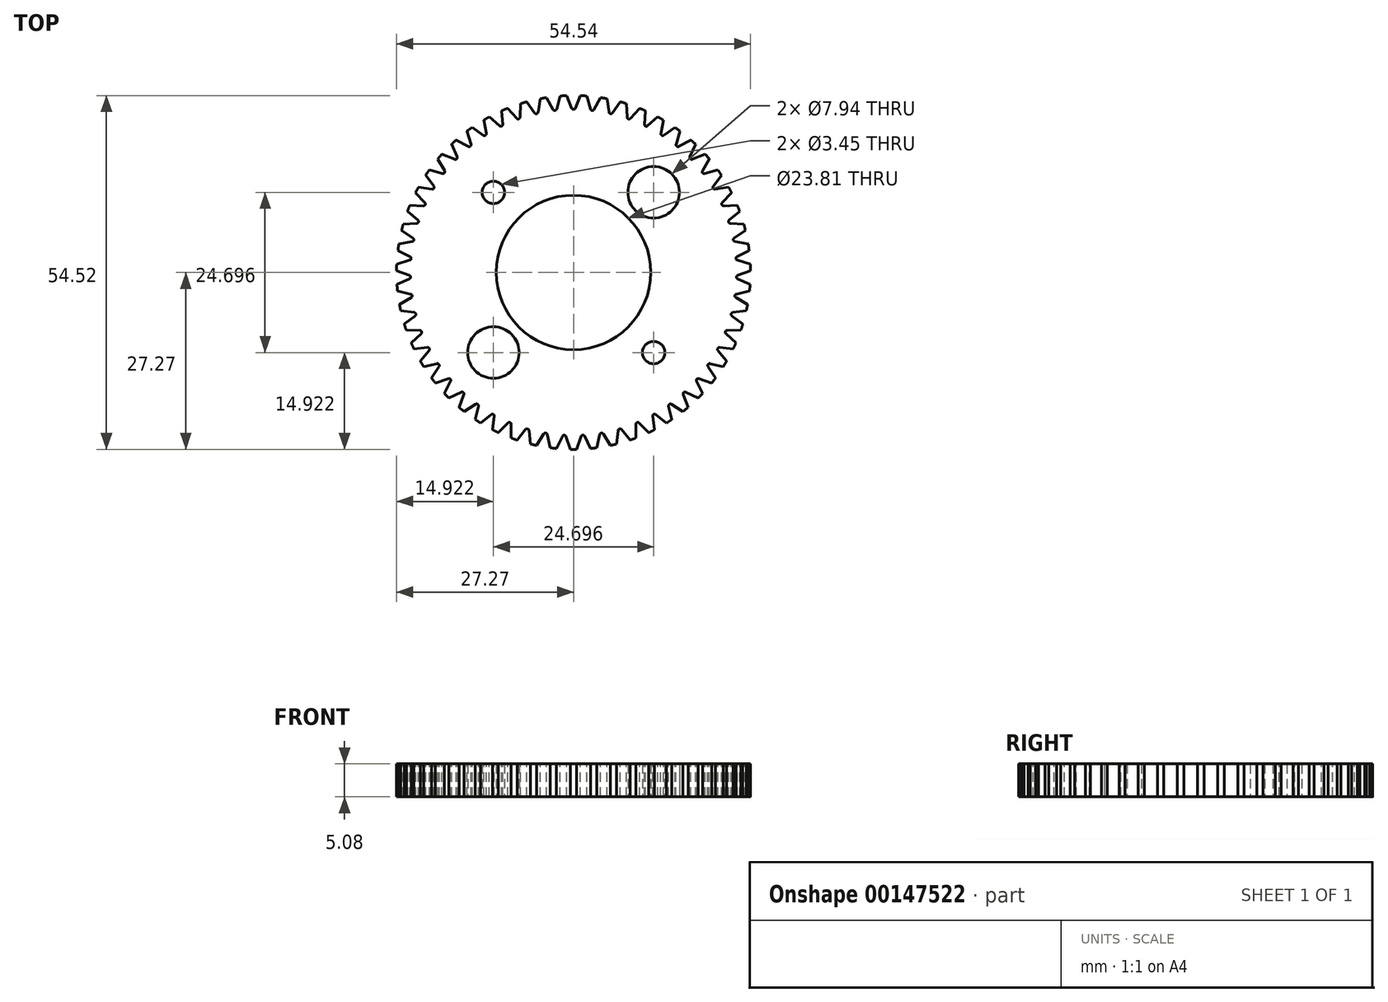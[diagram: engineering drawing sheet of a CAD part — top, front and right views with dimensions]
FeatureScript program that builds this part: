
annotation { "Feature Type Name" : "Feature", "Feature Type Description" : "" }
export const myFeature = defineFeature(function(context is Context, id is Id, definition is map)
    precondition{}
    {
        {
            var Q0;
            Q0=qCreatedBy(makeId("Top.planeOp"),FACE);
            var sketch = newSketch(context, id + "F0", { "sketchPlane" : qUnion([Q0])});
            skCircle(sketch, "E0", {"center": v(0, 0) * mm, "radius": 27.27 * mm});
            skCircle(sketch, "E1", {"center": v(0, 0) * mm, "radius": 11.9 * mm});
            skLineSegment(sketch, "E2.bottom", {"start": v(12.35, -12.35) * mm, "end": v(-12.35, -12.35) * mm, "construction": true});
            skLineSegment(sketch, "E2.top", {"start": v(12.35, 12.35) * mm, "end": v(-12.35, 12.35) * mm, "construction": true});
            skLineSegment(sketch, "E2.left", {"start": v(12.35, -12.35) * mm, "end": v(12.35, 12.35) * mm, "construction": true});
            skLineSegment(sketch, "E2.right", {"start": v(-12.35, -12.35) * mm, "end": v(-12.35, 12.35) * mm, "construction": true});
            skCircle(sketch, "E3", {"center": v(12.35, -12.35) * mm, "radius": 5.56 * mm, "construction": true});
            skCircle(sketch, "E4", {"center": v(12.35, 12.35) * mm, "radius": 3.97 * mm});
            skCircle(sketch, "E5", {"center": v(-12.35, -12.35) * mm, "radius": 3.97 * mm});
            skCircle(sketch, "E6", {"center": v(12.35, -12.35) * mm, "radius": 1.73 * mm});
            skCircle(sketch, "E7", {"center": v(-12.35, 12.35) * mm, "radius": 1.73 * mm});
            skSolve(sketch);
        }
        {
            var Q0;
            Q0=qSketchRegion(id+"F0",true);
            extrude(context, id + "F1", {"entities" : qUnion([Q0]), "depth" : 5.08 * mm});
        }
        {
            var Q0;
            Q0=makeQuery(id+"F1.opExtrude","CAP_FACE",FACE,{"disambiguationData":[OSD([sQuery(id+"F0.wireOp",EDGE,"E0")])],"isStart":false});
            var sketch = newSketch(context, id + "F2", { "sketchPlane" : qUnion([Q0])});
            skLineSegment(sketch, "E8", {"start": v(0, 0) * mm, "end": v(0, 27.27) * mm});
            skArc(sketch, "E9", {"start": v(1.06, 27.25) * mm, "mid": v(0, 27.27) * mm, "end": v(-1.06, 27.25) * mm});
            skLineSegment(sketch, "E10", {"start": v(-1.06, 27.25) * mm, "end": v(-0.28, 25.31) * mm});
            skLineSegment(sketch, "E11", {"start": v(1.06, 27.25) * mm, "end": v(0.28, 25.31) * mm});
            skArc(sketch, "E12", {"start": v(-0.28, 25.31) * mm, "mid": v(0, 25.13) * mm, "end": v(0.28, 25.31) * mm});
            skLineSegment(sketch, "E13", {"start": v(0, 0) * mm, "end": v(0.7, 27.27) * mm, "construction": true});
            skPoint(sketch, "E14", {"position": v(0.67, 26.28) * mm});
            skSolve(sketch);
        }
        {
            var Q0;
            Q0=qSketchRegion(id+"F2",true);
            var Q1;
            Q1=makeQuery(id+"F1.opExtrude","CAP_FACE",FACE,{"disambiguationData":[OSD([sQuery(id+"F0.wireOp",EDGE,"E0")])],"isStart":true});
            extrude(context, id + "F3", {"entities" : qUnion([Q0]), "operationType" : NewBodyOperationType.REMOVE, "endBound" : BoundingType.UP_TO_SURFACE, "oppositeDirection" : true, "endBoundEntityFace" : qUnion([Q1]), "depth" : 25.4 * mm});
        }
        {
            var Q0;
            Q0=makeQuery(id+"F3.boolean.opBoolean","COPY",FACE,{"derivedFrom":makeQuery(id+"F3.opExtrude","SWEPT_FACE",FACE,{"disambiguationData":[OSD([sQuery(id+"F2.wireOp",EDGE,"E11")])]})});
            var Q1;
            Q1=makeQuery(id+"F3.boolean.opBoolean","COPY",FACE,{"derivedFrom":makeQuery(id+"F3.opExtrude","SWEPT_FACE",FACE,{"disambiguationData":[OSD([sQuery(id+"F2.wireOp",EDGE,"E12")])]})});
            var Q2;
            Q2=makeQuery(id+"F3.boolean.opBoolean","COPY",FACE,{"derivedFrom":makeQuery(id+"F3.opExtrude","SWEPT_FACE",FACE,{"disambiguationData":[OSD([sQuery(id+"F2.wireOp",EDGE,"E10")])]})});
            var Q3;
            Q3=makeQuery(id+"F1.opExtrude","SWEPT_FACE",FACE,{"disambiguationData":[OSD([sQuery(id+"F0.wireOp",EDGE,"E0")])]});
            circularPattern(context, id + "F4", {"patternType" : PatternType.FACE, "faces" : qUnion([Q0, Q1, Q2]), "axis" : qUnion([Q3]), "angle" : 6.55 * degree, "instanceCount" : 55});
        }
    });
